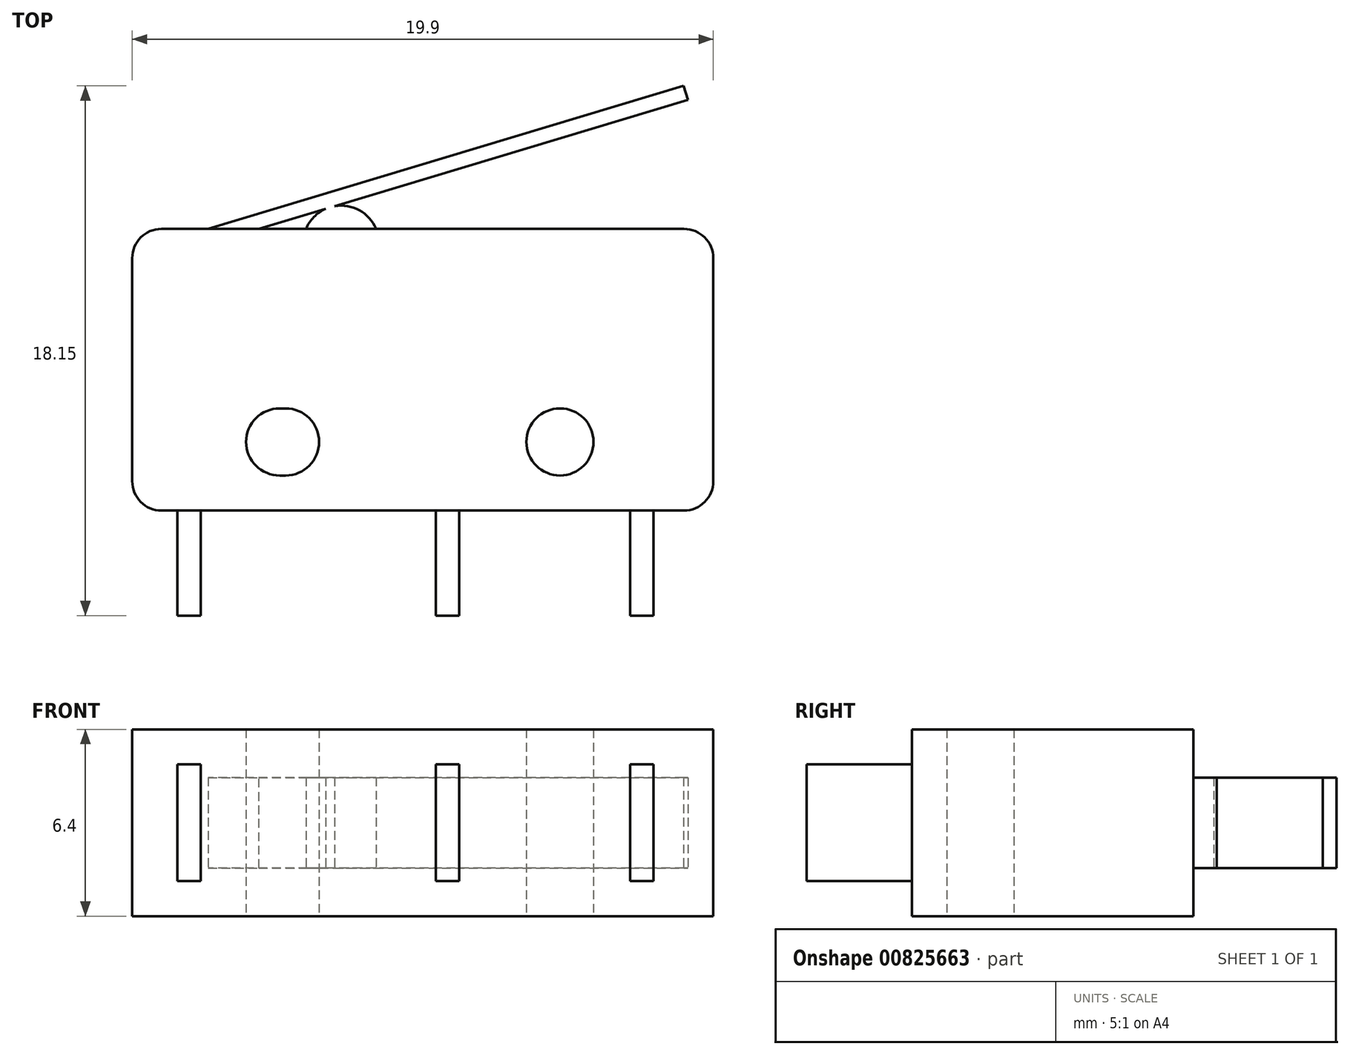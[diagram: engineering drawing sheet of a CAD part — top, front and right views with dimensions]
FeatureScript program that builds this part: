
annotation { "Feature Type Name" : "Feature", "Feature Type Description" : "" }
export const myFeature = defineFeature(function(context is Context, id is Id, definition is map)
    precondition{}
    {
        {
            var Q0;
            Q0=qCreatedBy(makeId("Top.planeOp"),FACE);
            var sketch = newSketch(context, id + "F0", { "sketchPlane" : qUnion([Q0])});
            skLineSegment(sketch, "E0.bottom", {"start": v(1, 0) * mm, "end": v(18.9, 0) * mm});
            skLineSegment(sketch, "E0.top", {"start": v(1, 9.65) * mm, "end": v(18.9, 9.65) * mm});
            skLineSegment(sketch, "E0.left", {"start": v(0, 1) * mm, "end": v(0, 8.65) * mm});
            skLineSegment(sketch, "E0.right", {"start": v(19.9, 1) * mm, "end": v(19.9, 8.65) * mm});
            skPoint(sketch, "E1.visualSharp", {"position": v(0, 0) * mm});
            skArc(sketch, "E1.filletArc", {"start": v(0, 1) * mm, "mid": v(0.3, 0.3) * mm, "end": v(1, 0) * mm});
            skPoint(sketch, "E2.visualSharp", {"position": v(0, 9.65) * mm});
            skArc(sketch, "E2.filletArc", {"start": v(1, 9.65) * mm, "mid": v(0.3, 9.36) * mm, "end": v(0, 8.65) * mm});
            skPoint(sketch, "E3.visualSharp", {"position": v(19.9, 9.65) * mm});
            skArc(sketch, "E3.filletArc", {"start": v(19.9, 8.65) * mm, "mid": v(19.6, 9.36) * mm, "end": v(18.9, 9.65) * mm});
            skPoint(sketch, "E4.visualSharp", {"position": v(19.9, 0) * mm});
            skArc(sketch, "E4.filletArc", {"start": v(18.9, 0) * mm, "mid": v(19.6, 0.3) * mm, "end": v(19.9, 1) * mm});
            skCircle(sketch, "E5", {"center": v(14.65, 2.35) * mm, "radius": 1.15 * mm});
            skArc(sketch, "E6", {"start": v(5.05, 3.5) * mm, "mid": v(3.9, 2.35) * mm, "end": v(5.05, 1.2) * mm});
            skArc(sketch, "E7", {"start": v(5.25, 1.2) * mm, "mid": v(6.4, 2.35) * mm, "end": v(5.25, 3.5) * mm});
            skLineSegment(sketch, "E8", {"start": v(14.65, 2.35) * mm, "end": v(5.05, 2.35) * mm, "construction": true});
            skLineSegment(sketch, "E9", {"start": v(5.25, 2.35) * mm, "end": v(5.05, 2.35) * mm, "construction": true});
            skPoint(sketch, "E10", {"position": v(5.15, 2.35) * mm});
            skLineSegment(sketch, "E11", {"start": v(5.05, 3.5) * mm, "end": v(5.25, 3.5) * mm});
            skLineSegment(sketch, "E12", {"start": v(5.05, 1.2) * mm, "end": v(5.25, 1.2) * mm});
            skSolve(sketch);
        }
        {
            var Q0;
            Q0 = qSketchRegion(id + "F0", true);
            extrude(context, id + "F1", {"entities" : qUnion([Q0]), "endBound" : BoundingType.SYMMETRIC, "depth" : 6.4 * mm, "offsetDistance" : 25 * mm});
        }
        {
            var Q0;
            Q0=qCreatedBy(makeId("Top.planeOp"),FACE);
            var sketch = newSketch(context, id + "F2", { "sketchPlane" : qUnion([Q0])});
            skCircle(sketch, "E13.0", {"center": v(14.65, 2.35) * mm, "radius": 1.15 * mm, "construction": true});
            skLineSegment(sketch, "E14", {"start": v(7.15, 13.74) * mm, "end": v(7.15, 9.15) * mm, "construction": true});
            skArc(sketch, "E15", {"start": v(8.35, 9.65) * mm, "mid": v(7.15, 10.45) * mm, "end": v(5.95, 9.65) * mm});
            skLineSegment(sketch, "E16.0", {"start": v(1, 9.65) * mm, "end": v(18.9, 9.65) * mm, "construction": true});
            skLineSegment(sketch, "E17", {"start": v(5.95, 9.65) * mm, "end": v(8.35, 9.65) * mm});
            skSolve(sketch);
        }
        {
            var Q0;
            Q0 = qSketchRegion(id + "F2", true);
            extrude(context, id + "F3", {"entities" : qUnion([Q0]), "operationType" : NewBodyOperationType.ADD, "endBound" : BoundingType.SYMMETRIC, "depth" : 3.1 * mm, "offsetDistance" : 25 * mm});
        }
        {
            var Q0;
            Q0=qCreatedBy(makeId("Top.planeOp"),FACE);
            var sketch = newSketch(context, id + "F4", { "sketchPlane" : qUnion([Q0])});
            skCircle(sketch, "E18.0", {"center": v(14.65, 2.35) * mm, "radius": 1.15 * mm, "construction": true});
            skLineSegment(sketch, "E19.bottom", {"start": v(17.05, 0) * mm, "end": v(17.85, 0) * mm});
            skLineSegment(sketch, "E19.top", {"start": v(17.05, -3.6) * mm, "end": v(17.85, -3.6) * mm});
            skLineSegment(sketch, "E19.left", {"start": v(17.05, 0) * mm, "end": v(17.05, -3.6) * mm});
            skLineSegment(sketch, "E19.right", {"start": v(17.85, 0) * mm, "end": v(17.85, -3.6) * mm});
            skLineSegment(sketch, "E20.bottom", {"start": v(10.4, 0) * mm, "end": v(11.2, 0) * mm});
            skLineSegment(sketch, "E20.top", {"start": v(10.4, -3.6) * mm, "end": v(11.2, -3.6) * mm});
            skLineSegment(sketch, "E20.left", {"start": v(10.4, 0) * mm, "end": v(10.4, -3.6) * mm});
            skLineSegment(sketch, "E20.right", {"start": v(11.2, 0) * mm, "end": v(11.2, -3.6) * mm});
            skLineSegment(sketch, "E21.bottom", {"start": v(1.55, 0) * mm, "end": v(2.35, 0) * mm});
            skLineSegment(sketch, "E21.top", {"start": v(1.55, -3.6) * mm, "end": v(2.35, -3.6) * mm});
            skLineSegment(sketch, "E21.left", {"start": v(1.55, 0) * mm, "end": v(1.55, -3.6) * mm});
            skLineSegment(sketch, "E21.right", {"start": v(2.35, 0) * mm, "end": v(2.35, -3.6) * mm});
            skSolve(sketch);
        }
        {
            var Q0;
            Q0 = qSketchRegion(id + "F4", true);
            extrude(context, id + "F5", {"entities" : qUnion([Q0]), "operationType" : NewBodyOperationType.ADD, "endBound" : BoundingType.SYMMETRIC, "depth" : 4 * mm, "offsetDistance" : 25 * mm});
        }
        {
            var Q0;
            Q0=qCreatedBy(makeId("Top.planeOp"),FACE);
            var sketch = newSketch(context, id + "F6", { "sketchPlane" : qUnion([Q0])});
            skCircle(sketch, "E22.0", {"center": v(14.65, 2.35) * mm, "radius": 1.15 * mm, "construction": true});
            skLineSegment(sketch, "E23", {"start": v(1.22, 14.55) * mm, "end": v(18.88, 14.55) * mm, "construction": true});
            skCircle(sketch, "E24", {"center": v(1.95, 8.45) * mm, "radius": 18 * mm, "construction": true});
            skLineSegment(sketch, "E25", {"start": v(18.88, 14.55) * mm, "end": v(1.65, 9.36) * mm});
            skLineSegment(sketch, "E26", {"start": v(1.65, 9.36) * mm, "end": v(1.8, 8.89) * mm});
            skLineSegment(sketch, "E27", {"start": v(1.8, 8.89) * mm, "end": v(19.03, 14.07) * mm});
            skLineSegment(sketch, "E28", {"start": v(19.03, 14.07) * mm, "end": v(18.88, 14.55) * mm});
            skArc(sketch, "E29.0", {"start": v(8.35, 9.65) * mm, "mid": v(7.15, 10.45) * mm, "end": v(5.95, 9.65) * mm, "construction": true});
            skCircle(sketch, "E30", {"center": v(7.15, 9.15) * mm, "radius": 1.29 * mm, "construction": true});
            skSolve(sketch);
        }
        {
            var Q0;
            Q0 = qSketchRegion(id + "F6", true);
            extrude(context, id + "F7", {"entities" : qUnion([Q0]), "operationType" : NewBodyOperationType.ADD, "endBound" : BoundingType.SYMMETRIC, "depth" : 3.1 * mm, "offsetDistance" : 25 * mm});
        }
    });
